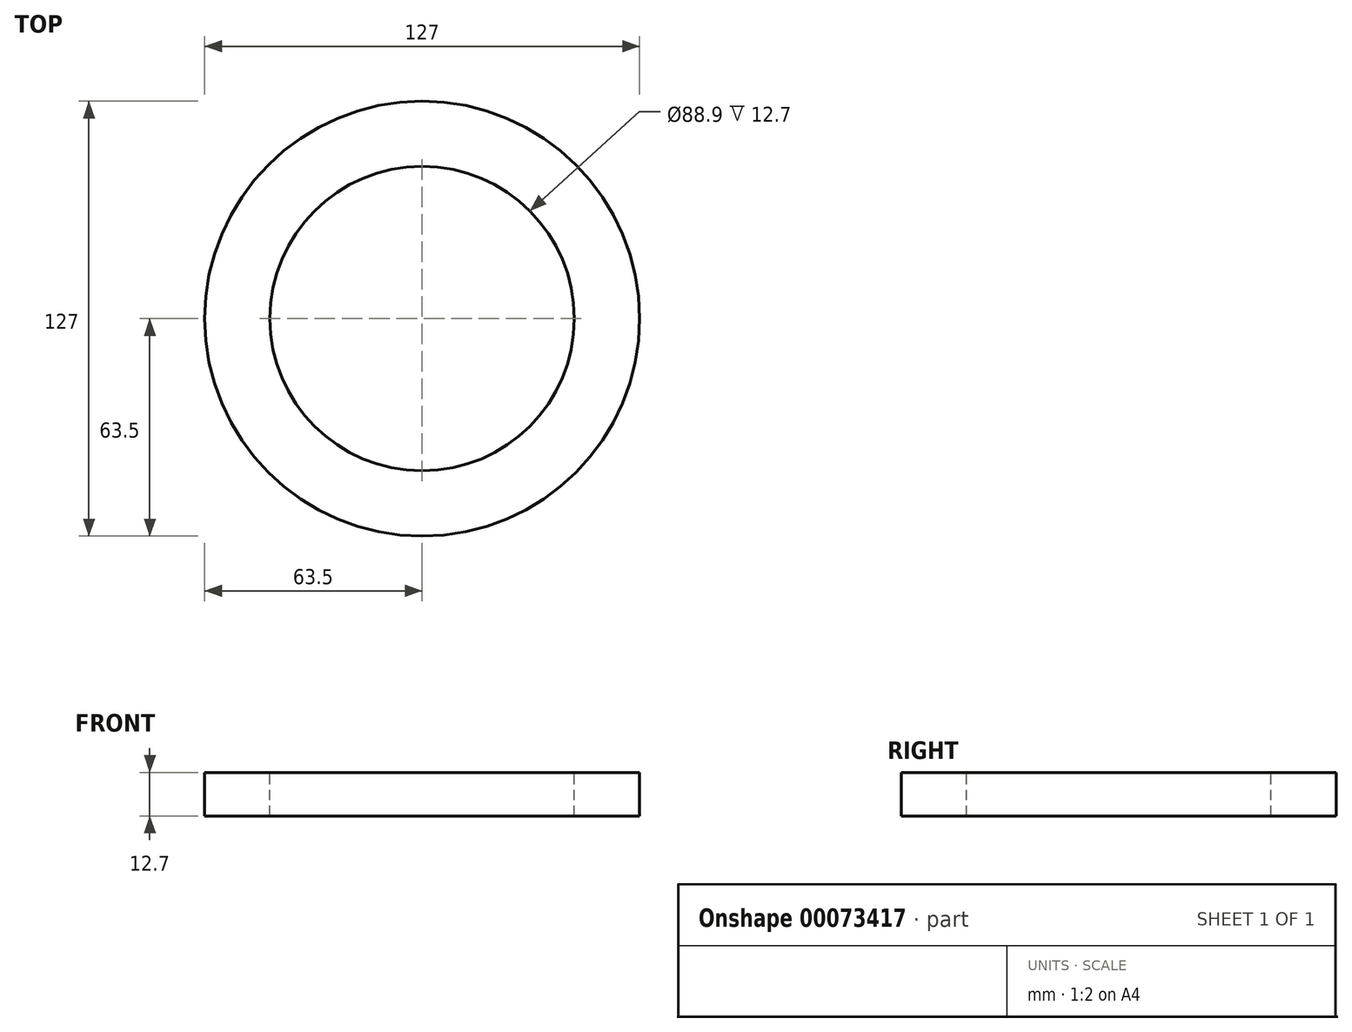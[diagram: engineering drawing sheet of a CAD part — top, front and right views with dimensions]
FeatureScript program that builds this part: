
annotation { "Feature Type Name" : "Feature", "Feature Type Description" : "" }
export const myFeature = defineFeature(function(context is Context, id is Id, definition is map)
    precondition{}
    {
        {
            var Q0;
            Q0=qCreatedBy(makeId("Top.planeOp"),FACE);
            var sketch = newSketch(context, id + "F0", { "sketchPlane" : qUnion([Q0])});
            skCircle(sketch, "E0", {"center": v(0, 0) * mm, "radius": 63.5 * mm});
            skSolve(sketch);
        }
        {
            var Q0;
            Q0=makeQuery(id+"F0.imprint","IMPRINT",FACE,{"disambiguationData":[TD([[makeQuery(id+"F0.imprint","IMPRINT",EDGE,{"derivedFrom":sQuery(id+"F0.wireOp",EDGE,"E0")}),1.0]])]});
            extrude(context, id + "F1", {"entities" : qUnion([Q0]), "depth" : 12.7 * mm});
        }
        {
            var Q0;
            Q0=makeQuery(id+"F1.opExtrude","CAP_FACE",FACE,{"disambiguationData":[OSD([sQuery(id+"F0.wireOp",EDGE,"E0")])],"isStart":false});
            var sketch = newSketch(context, id + "F2", { "sketchPlane" : qUnion([Q0])});
            skCircle(sketch, "E1", {"center": v(0, 0) * mm, "radius": 44.45 * mm});
            skSolve(sketch);
        }
        {
            var Q0;
            Q0=makeQuery(id+"F2.imprint","IMPRINT",FACE,{"disambiguationData":[TD([[makeQuery(id+"F2.imprint","IMPRINT",EDGE,{"derivedFrom":sQuery(id+"F2.wireOp",EDGE,"E1")}),1.0]])]});
            extrude(context, id + "F3", {"entities" : qUnion([Q0]), "operationType" : NewBodyOperationType.REMOVE, "endBound" : BoundingType.THROUGH_ALL, "oppositeDirection" : true, "depth" : 25.4 * mm});
        }
    });
